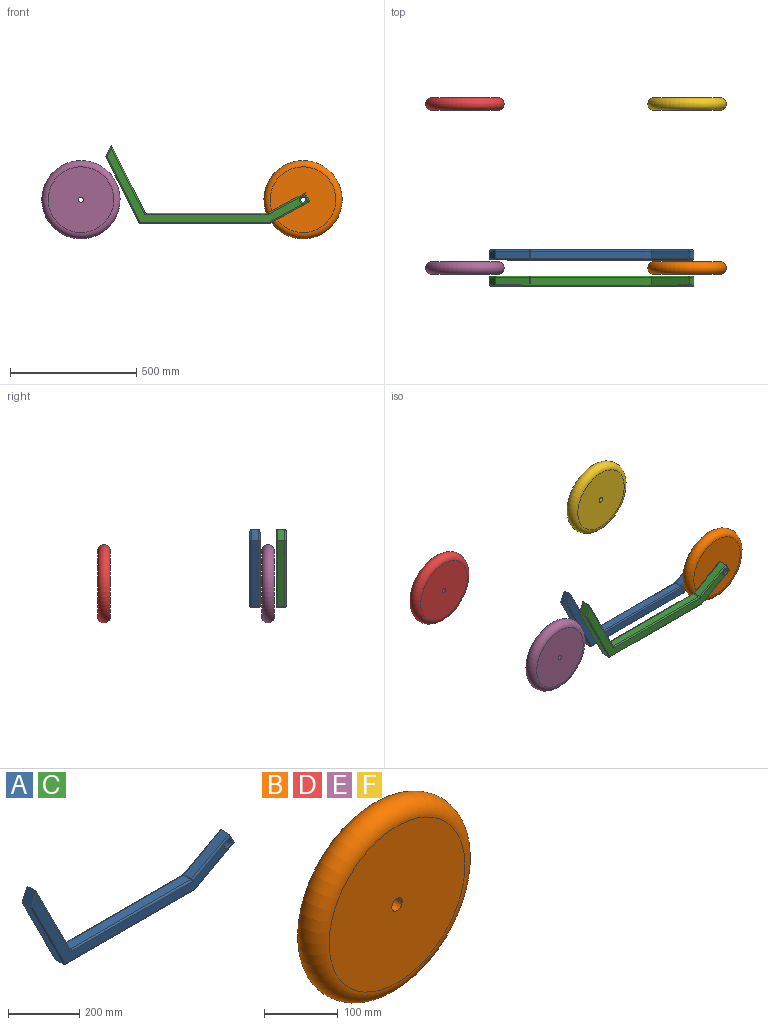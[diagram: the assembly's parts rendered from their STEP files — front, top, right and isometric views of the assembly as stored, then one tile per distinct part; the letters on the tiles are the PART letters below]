
ASSEMBLY  parts=6 mates=5
PART A: 45 faces, bbox 809x40x309.6 mm
  f0: plane 783.49x293.23mm, normal (0,-1,0), area 28077.4mm2, adj f16,f18,f19,f23,f27,f28,f32,f36
  f1: plane 20.33x13.2mm, normal (0,-1,0), area 48.3mm2, adj f24,f28,f44
  f2: plane 783.49x293.23mm, normal (0,1,0), area 28077.4mm2, adj f17,f20,f21,f26,f30,f31,f35,f38
  f3: plane 20.33x13.2mm, normal (0,1,0), area 48.3mm2, adj f20,f25,f43
  f4: plane 157.3x85mm, normal (0.48,0,-0.88), area 5363.8mm2, adj f5,f28,f29,f30
  f5: plane 35.19x30mm, normal (0.88,0,0.48), area 1200mm2, adj f4,f6,f24,f25
  f6: plane 148.4x80.19mm, normal (-0.48,0,0.88), area 5060.3mm2, adj f5,f15,f19,f20
  f7: plane 478.3x30mm, normal (0,0,1), area 14348.9mm2, adj f15,f18,f21,f22
  f8: plane 266.87x134.81mm, normal (0.89,0,0.45), area 8969.7mm2, adj f9,f22,f27,f31
  f9: plane 45.82x30mm, normal (-0.9,0,0.43), area 1520.6mm2, adj f8,f10,f32,f35
  f10: plane 261.05x131.87mm, normal (-0.89,0,-0.45), area 8773.9mm2, adj f9,f36,f39,f42
  f11: plane 513.02x30mm, normal (0,0,-1), area 15390.6mm2, adj f29,f37,f38,f42
  f12: cylinder r=10mm len=30mm, axis (0,1,0), area 1885mm2, adj f43,f44
  f13: plane 20.33x13.2mm, normal (0,-1,0), area 48.3mm2, adj f19,f24,f44
  f14: plane 20.33x13.2mm, normal (0,1,0), area 48.3mm2, adj f25,f30,f43
  f15: cylinder r=5mm len=30mm, axis (0,-1,0), area 74.3mm2, adj f6,f7,f16,f17
  f16: torus R=10mm, axis (0,-1,0), area 26.5mm2, adj f0,f15,f18,f19
  f17: torus R=10mm, axis (0,-1,0), area 26.5mm2, adj f2,f15,f20,f21
  f18: cylinder r=5mm len=478.3mm, axis (1,0,0), area 3756.5mm2, adj f0,f7,f16,f23
  f19: cylinder r=5mm len=150.77mm, axis (0.88,0,0.48), area 1310.5mm2, adj f0,f6,f13,f16,f24
  f20: cylinder r=5mm len=150.77mm, axis (-0.88,0,-0.48), area 1310.5mm2, adj f2,f3,f6,f17,f25
  f21: cylinder r=5mm len=478.3mm, axis (-1,0,0), area 3756.5mm2, adj f2,f7,f17,f26
  f22: cylinder r=5mm len=30mm, axis (0,-1,0), area 165.5mm2, adj f7,f8,f23,f26
  f23: torus R=10mm, axis (0,-1,0), area 59.1mm2, adj f0,f18,f22,f27
  f24: cylinder r=5mm len=37.57mm, axis (0.48,0,-0.88), area 285.6mm2, adj f1,f5,f13,f19,f28
  f25: cylinder r=5mm len=37.57mm, axis (-0.48,0,0.88), area 285.6mm2, adj f3,f5,f14,f20,f30
  f26: torus R=10mm, axis (0,-1,0), area 59.1mm2, adj f2,f21,f22,f31
  f27: cylinder r=5mm len=269.13mm, axis (0.45,0,-0.89), area 2319.1mm2, adj f0,f8,f23,f32
  f28: cylinder r=5mm len=159.67mm, axis (-0.88,0,-0.48), area 1390mm2, adj f0,f1,f4,f24,f33
  f29: cylinder r=5mm len=30mm, axis (0,1,0), area 74.3mm2, adj f4,f11,f33,f34
  f30: cylinder r=5mm len=159.67mm, axis (0.88,0,0.48), area 1390mm2, adj f2,f4,f14,f25,f34
  f31: cylinder r=5mm len=269.13mm, axis (-0.45,0,0.89), area 2319.1mm2, adj f2,f8,f26,f35
  f32: cylinder r=5mm len=47.96mm, axis (0.43,0,0.9), area 361.9mm2, adj f0,f9,f27,f36
  f33: sphere r=5mm, area 12.4mm2, adj f28,f29,f37
  f34: sphere r=5mm, area 12.4mm2, adj f29,f30,f38
  f35: cylinder r=5mm len=47.96mm, axis (-0.43,0,-0.9), area 361.9mm2, adj f2,f9,f31,f39
  f36: cylinder r=5mm len=263.3mm, axis (-0.45,0,0.89), area 2290mm2, adj f0,f10,f32,f40
  f37: cylinder r=5mm len=513.02mm, axis (-1,0,0), area 4029.3mm2, adj f0,f11,f33,f40
  f38: cylinder r=5mm len=513.02mm, axis (1,0,0), area 4029.3mm2, adj f2,f11,f34,f41
  f39: cylinder r=5mm len=263.3mm, axis (0.45,0,-0.89), area 2290mm2, adj f2,f10,f35,f41
  f40: sphere r=5mm, area 27.6mm2, adj f36,f37,f42
  f41: sphere r=5mm, area 27.6mm2, adj f38,f39,f42
  f42: cylinder r=5mm len=30mm, axis (0,1,0), area 165.5mm2, adj f10,f11,f40,f41
  f43: torus R=15mm, axis (0,-1,0), area 583.1mm2, adj f2,f3,f12,f14
  f44: torus R=15mm, axis (0,-1,0), area 583.1mm2, adj f0,f1,f12,f13
PART B: 4 faces, bbox 335.5x50x335.5 mm
  f0: plane 260x260mm, normal (0,-1,0), area 52778.8mm2, adj f2,f3
  f1: plane 260x260mm, normal (0,1,0), area 52778.8mm2, adj f2,f3
  f2: torus R=130mm, axis (0,-1,0), area 72006.4mm2, adj f0,f1
  f3: cylinder r=10mm len=50mm, axis (0,-1,0), area 3141.6mm2, adj f0,f1
PART C: same geometry as A
PART D: same geometry as B
PART E: same geometry as B
PART F: same geometry as B
PLACE A t=(154.61,63.97,-1.84)mm
PLACE B t=(921.57,16.97,7.01)mm
PLACE C t=(154.61,-40.03,-1.84)mm
PLACE D t=(41.57,666.97,7.01)mm
PLACE E t=(41.57,16.97,7.01)mm
PLACE F t=(921.57,666.97,7.01)mm
MATE fastened C.f12 <-> B.f2  axis (0,-1,0) through (921.57,-75.03,7.01)mm
MATE fastened A.f12 <-> C.f12  axis (0,-1,0) through (921.57,23.97,7.01)mm
MATE fastened E.f2 <-> D.f3  axis (0,1,0) through (41.57,16.97,7.01)mm
MATE fastened F.f3 <-> B.f2  axis (0,-1,0) through (921.57,616.97,7.01)mm
MATE fastened B.f2 <-> E.f0  axis (0,-1,0) through (921.57,-33.03,7.01)mm
